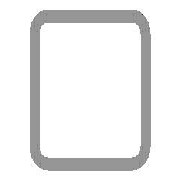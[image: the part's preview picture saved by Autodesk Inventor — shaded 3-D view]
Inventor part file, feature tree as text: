
AUTODESK INVENTOR PART (.ipt)
format: ipt  version: 2025.3 (Build 293356000, 356)  size: 145,920 bytes
history: native  units: mm (DEFAULTED — no unit token found)
features: other x4, plane x3, split x2, sketch x1
ambient origin geometry x8: Origin, YZ Plane, XZ Plane, XY Plane, X Axis, Y Axis, Z Axis, Center Point
bodies: Solid1 (feature_tree), Body (feature_tree)
feature tree (10):
  parser-record x1  (decoder bookkeeping rows leaked as tree rows — omitted from the tree; the rows remain in map.json)
  other  "Driven Length"
  other  "Start Plane"
  other  "End Plane"
  plane  "Work Plane4"
  split  "Split1"
  plane  "Work Plane5"
  split  "Split2"
  sketch  "Sketch3"  dims[d3=2366.612931mm d4=0.0mm d7=6.0mm d9=80.0mm d11=80.0mm d12=3.0mm d13=153.387069mm d14=2520.0mm d15=40.0mm d16=40.0mm d17=90.0deg d18=2366.612931mm]
  plane  "Work Plane3"
